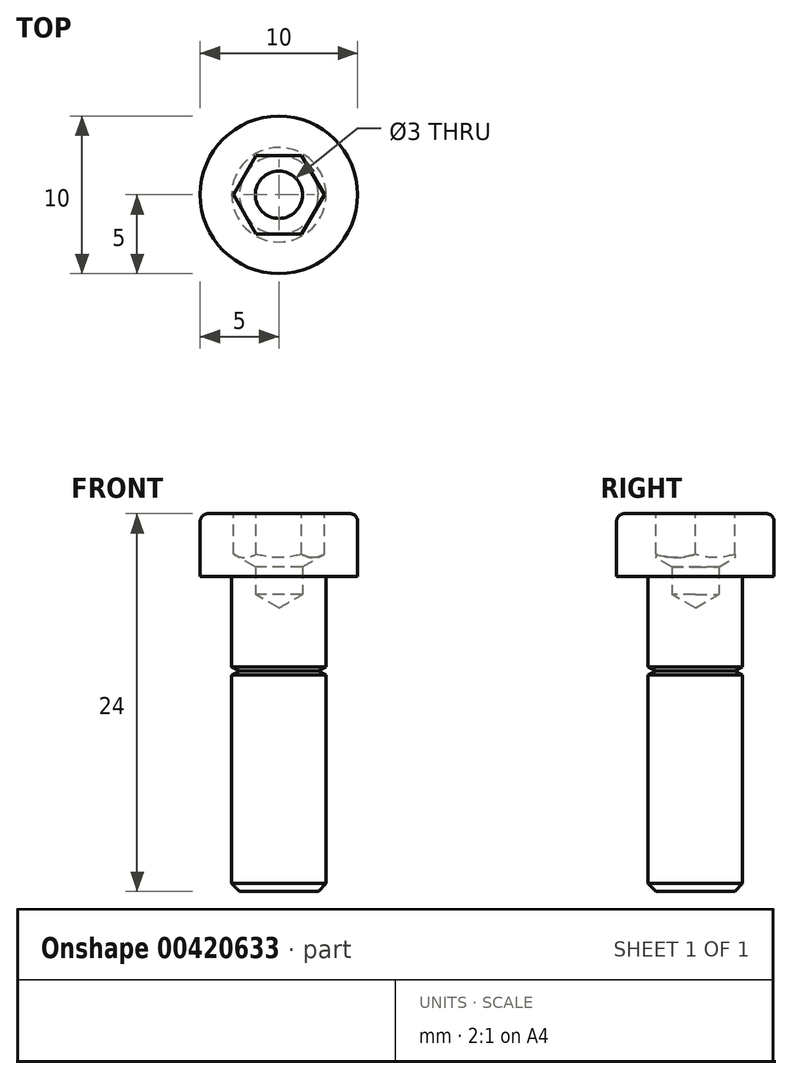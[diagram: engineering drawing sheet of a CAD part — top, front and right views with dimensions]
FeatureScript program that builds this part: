
annotation { "Feature Type Name" : "Feature", "Feature Type Description" : "" }
export const myFeature = defineFeature(function(context is Context, id is Id, definition is map)
    precondition{}
    {
        {
            var Q0;
            Q0=qCreatedBy(makeId("Front.planeOp"),FACE);
            var sketch = newSketch(context, id + "F0", { "sketchPlane" : qUnion([Q0])});
            skLineSegment(sketch, "E0", {"start": v(0, 0) * mm, "end": v(0, 36.66) * mm, "construction": true});
            skLineSegment(sketch, "E1", {"start": v(0, 0) * mm, "end": v(-3, 0) * mm});
            skLineSegment(sketch, "E2", {"start": v(-3, 0) * mm, "end": v(-3, 20) * mm, "construction": true});
            skLineSegment(sketch, "E3", {"start": v(-3, 20) * mm, "end": v(-5, 20) * mm});
            skLineSegment(sketch, "E4", {"start": v(-5, 20) * mm, "end": v(-5, 24) * mm});
            skLineSegment(sketch, "E5", {"start": v(-5, 24) * mm, "end": v(0, 24) * mm, "construction": true});
            skLineSegment(sketch, "E6", {"start": v(-1.5, 24) * mm, "end": v(-1.5, 18.87) * mm});
            skLineSegment(sketch, "E7", {"start": v(-1.5, 18.87) * mm, "end": v(0, 18) * mm});
            skLineSegment(sketch, "E8", {"start": v(0, 18) * mm, "end": v(0, 0) * mm});
            skLineSegment(sketch, "E9", {"start": v(-1.5, 24) * mm, "end": v(-5, 24) * mm});
            skLineSegment(sketch, "E10", {"start": v(-3, 14.25) * mm, "end": v(-2.5, 14) * mm});
            skLineSegment(sketch, "E11", {"start": v(-2.5, 14) * mm, "end": v(-3, 13.75) * mm});
            skLineSegment(sketch, "E12", {"start": v(-3, 13.75) * mm, "end": v(-3, 0) * mm});
            skLineSegment(sketch, "E13", {"start": v(-3, 14.25) * mm, "end": v(-3, 20) * mm});
            skSolve(sketch);
        }
        {
            var Q0;
            Q0 = qSketchRegion(id + "F0", true);
            var Q1;
            Q1=sQuery(id+"F0.wireOp",EDGE,"E0");
            revolve(context, id + "F1", {"entities" : qUnion([Q0]), "axis" : qUnion([Q1]), "revolveType" : RevolveType.FULL});
        }
        {
            var Q0;
            Q0=makeQuery(id+"F1.opRevolve","SWEPT_EDGE",EDGE,{"disambiguationData":[OSD([sQuery(id+"F0.wireOp",EDGE,"E4"),sQuery(id+"F0.wireOp",EDGE,"E9")])]});
            fillet(context, id + "F2", {"entities" : qUnion([Q0]), "radius" : 0.5 * mm, "tangentPropagation" : true, "allowEdgeOverflow" : false});
        }
        {
            var Q0;
            Q0=makeQuery(id+"F1.opRevolve","SWEPT_EDGE",EDGE,{"disambiguationData":[OSD([sQuery(id+"F0.wireOp",EDGE,"E1"),sQuery(id+"F0.wireOp",EDGE,"E2")])]});
            chamfer(context, id + "F3", {"entities" : qUnion([Q0]), "width" : 0.5 * mm, "tangentPropagation" : true});
        }
        {
            var Q0;
            Q0=makeQuery(id+"F1.opRevolve","SWEPT_FACE",FACE,{"disambiguationData":[OSD([sQuery(id+"F0.wireOp",EDGE,"E9")])]});
            var sketch = newSketch(context, id + "F4", { "sketchPlane" : qUnion([Q0])});
            skCircle(sketch, "E14.cCircle", {"center": v(0, 0) * mm, "radius": 2.5 * mm, "construction": true});
            skLineSegment(sketch, "E14.0", {"start": v(1.44, -2.5) * mm, "end": v(-1.44, -2.5) * mm});
            skLineSegment(sketch, "E14.1", {"start": v(-1.44, -2.5) * mm, "end": v(-2.89, 0) * mm});
            skLineSegment(sketch, "E14.2", {"start": v(-2.89, 0) * mm, "end": v(-1.44, 2.5) * mm});
            skLineSegment(sketch, "E14.3", {"start": v(-1.44, 2.5) * mm, "end": v(1.44, 2.5) * mm});
            skLineSegment(sketch, "E14.4", {"start": v(1.44, 2.5) * mm, "end": v(2.89, 0) * mm});
            skLineSegment(sketch, "E14.5", {"start": v(2.89, 0) * mm, "end": v(1.44, -2.5) * mm});
            skPoint(sketch, "E14.0.midPoint", {"position": v(0, -2.5) * mm});
            skSolve(sketch);
        }
        {
            var Q0;
            Q0 = qSketchRegion(id + "F4", true);
            extrude(context, id + "F5", {"entities" : qUnion([Q0]), "operationType" : NewBodyOperationType.REMOVE, "oppositeDirection" : true, "depth" : 2.38 * mm});
        }
        {
            var Q0;
            Q0=makeQuery(id+"F5.boolean.opBoolean","INTERSECT",EDGE,{"derivedFrom":[makeQuery(id+"F1.opRevolve","SWEPT_FACE",FACE,{"disambiguationData":[OSD([sQuery(id+"F0.wireOp",EDGE,"E6")])]}),makeQuery(id+"F5.opExtrude","CAP_FACE",FACE,{"disambiguationData":[OSD([sQuery(id+"F4.wireOp",EDGE,"E14.0"),sQuery(id+"F4.wireOp",EDGE,"E14.1"),sQuery(id+"F4.wireOp",EDGE,"E14.2"),sQuery(id+"F4.wireOp",EDGE,"E14.3"),sQuery(id+"F4.wireOp",EDGE,"E14.4"),sQuery(id+"F4.wireOp",EDGE,"E14.5")])],"isStart":false})]});
            chamfer(context, id + "F6", {"entities" : qUnion([Q0]), "chamferType" : ChamferType.OFFSET_ANGLE, "width" : 1 * mm, "oppositeDirection" : false, "angle" : 60 * degree, "tangentPropagation" : true});
        }
    });
